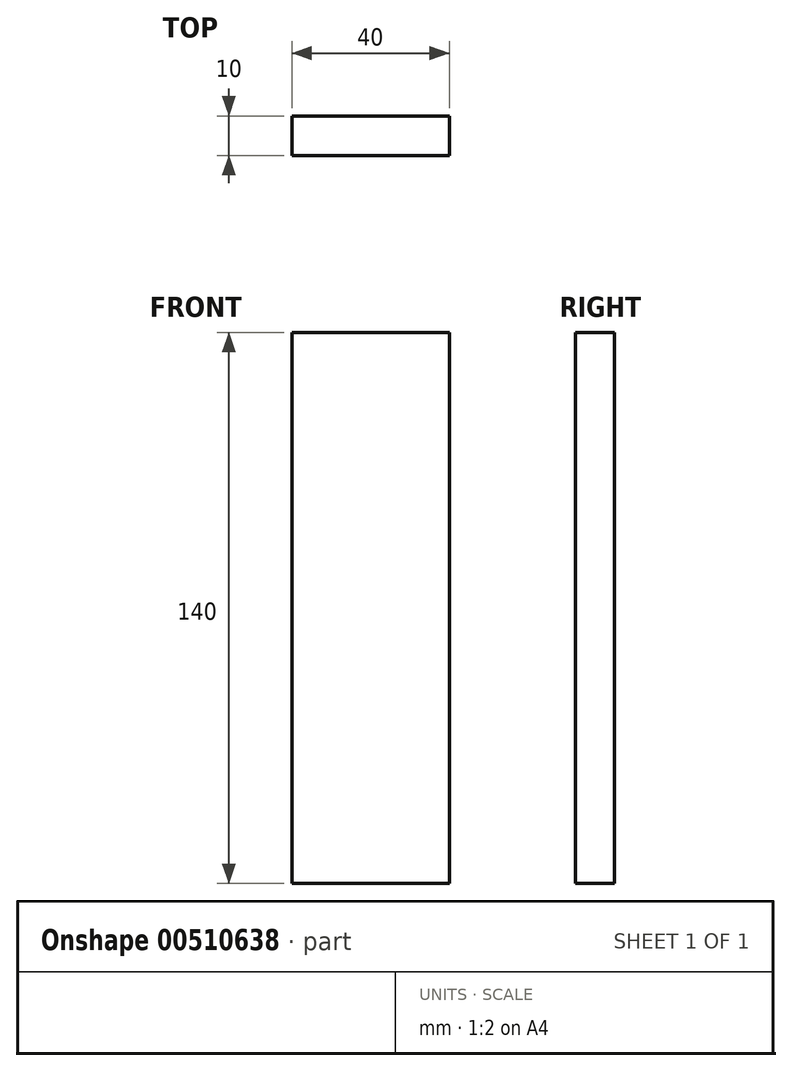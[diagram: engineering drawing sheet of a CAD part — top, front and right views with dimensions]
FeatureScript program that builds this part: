
annotation { "Feature Type Name" : "Feature", "Feature Type Description" : "" }
export const myFeature = defineFeature(function(context is Context, id is Id, definition is map)
    precondition{}
    {
        {
            var Q0;
            Q0=qCreatedBy(makeId("Top.planeOp"),FACE);
            var sketch = newSketch(context, id + "F0", { "sketchPlane" : qUnion([Q0])});
            skLineSegment(sketch, "E0.bottom", {"start": v(-20, 5) * mm, "end": v(20, 5) * mm});
            skLineSegment(sketch, "E0.top", {"start": v(-20, -5) * mm, "end": v(20, -5) * mm});
            skLineSegment(sketch, "E0.left", {"start": v(-20, 5) * mm, "end": v(-20, -5) * mm});
            skLineSegment(sketch, "E0.right", {"start": v(20, 5) * mm, "end": v(20, -5) * mm});
            skPoint(sketch, "E0.middle", {"position": v(0, 0) * mm});
            skSolve(sketch);
        }
        {
            var Q0;
            Q0 = qSketchRegion(id + "F0", true);
            extrude(context, id + "F1", {"entities" : qUnion([Q0]), "depth" : 140 * mm});
        }
    });
